# Revit family: CADS_AIRFLOWdev_AirTerminal_SquareExternalGrille_Intake
name_source: partatom
category: Air Terminals
revit_build: Autodesk Revit 2015 (Build: 20160512_0715(x64)
units: mm (PartAtom-declared; Revit-internal decimal feet)

## types (16) — shared parameters
6MonthlyMaintenance = Visually inspect system, clean the fan and ducting if necessary
AirflowRateRange = 0-61
AssetType = Fixed
B = 20 mm  [stored 0.0656168 ft]
CEApproval = Yes
Default Elevation = 1219 mm
DurationUnit = Years
Exclusions = Incorrect Use / Incorrect Installation / Installed by a non-accredited electrician. Customer abuse.
FaceType = LOUVERED
Finish = Matte
FlowControlType = NONE
Grade = Virgin
HasIntegralControl = No
HasSoundAttenuator = No
HasThermalInsulation = No
ISO140001 = Yes
ISO90001 = Yes
IsExtendedWarranty = No
Manufacturer = Airflow Developments Ltd
ManufacturerAddress = Aidelle House
Lancaster Road
Cressex Business Park
High Wycombe
Bucks
HP123QP
ManufacturerTelephone = 01494 525252
ManufacturerWebsite = www.airflow.com
Material = Plastic
MountingType = SURFACE
NBSCode = 90-75-50/370 Air terminals;
PointOfContact = Airflow Developments Ltd
ProductionYear = 2017
ServiceLifeDuration = 10
ServiceLifeType = EXPECTEDSERVICELIFE
Shape = Rectangular
Uniclass2015 = Pr_65_70_46_01
WarrantyContent = Replacement of part if faulty
WarrantyGuarantor = Airflow Developments Ltd
WarrantyPeriod = 2

## per-type parameters (varying)
| type | A | Color | Constituents | D | Description | Dv | External_Grille | Fly_Screen | GrossWeight | ModelLabel | ModelReference | NominalHeight | NominalLength | NominalWidth | NumberOfSlots | ReplacementCost | ShippingWeight | Size |
| 140 x 140 x 100mm Dia - White | 140 mm  [stored 0.459318 ft] | White | White | 100 mm  [stored 0.328084 ft] | 140 x 140 x 100mm dia. Fixed Grille (White) No F/S | 98 mm  [stored 0.321522 ft] | CADS_AirFlow_White | No | 0.01 kg | 140 x 140 x 100mm dia. Fixed Grille (White) No F/S | 52641101 | 140 mm  [stored 0.459318 ft] | 46 mm  [stored 0.150919 ft] | 140 mm  [stored 0.459318 ft] | 20 | 4.752 | 0.01 kg | 46 x 140 x 140 |
| 140 x 140 x 100mm Dia -  Grey | 140 mm  [stored 0.459318 ft] | Grey | Grey | 100 mm  [stored 0.328084 ft] | 140 x 140 x 100mm dia. Fixed Grille (Grey) No F/S | 98 mm  [stored 0.321522 ft] | CADS_AirFlow_Grey | No | 0.01 kg | 140 x 140 x 100mm dia. Fixed Grille (Grey) No F/S | 52641102 | 140 mm  [stored 0.459318 ft] | 46 mm  [stored 0.150919 ft] | 140 mm  [stored 0.459318 ft] | 20 | 4.752 | 0.01 kg | 46 x 140 x 140 |
| 140 x 140 x 100mm Dia - Terracotta | 140 mm  [stored 0.459318 ft] | Terracotta | Terracotta | 100 mm  [stored 0.328084 ft] | 140 x 140 x 100mm dia. Fixed Grille (Terracotta) No F/S | 98 mm  [stored 0.321522 ft] | CADS_AirFlow_Terracotta | No | 0.01 kg | 140 x 140 x 100mm dia. Fixed Grille (Terracotta) No F/S | 52641103 | 140 mm  [stored 0.459318 ft] | 46 mm  [stored 0.150919 ft] | 140 mm  [stored 0.459318 ft] | 20 | 4.752 | 0.01 kg | 46 x 140 x 140 |
| 140 x 140 x 100mm Dia - Brown | 140 mm  [stored 0.459318 ft] | Brown | Brown | 100 mm  [stored 0.328084 ft] | 140 x 140 x 100mm dia. Fixed Grille (Brown) No F/S | 98 mm  [stored 0.321522 ft] | CADS_AirFlow_Brown | No | 0.01 kg | 140 x 140 x 100mm dia. Fixed Grille (Brown) No F/S | 52641104 | 140 mm  [stored 0.459318 ft] | 46 mm  [stored 0.150919 ft] | 140 mm  [stored 0.459318 ft] | 20 | 4.752 | 0.01 kg | 46 x 140 x 140 |
| 140 x 140 x 100mm Dia - Beige | 140 mm  [stored 0.459318 ft] | Beige | Beige | 100 mm  [stored 0.328084 ft] | 140 x 140 x 100mm dia. Fixed Grille (Beige) No F/S | 98 mm  [stored 0.321522 ft] | CADS_AirFlow_Beige | No | 0.01 kg | 140 x 140 x 100mm dia. Fixed Grille (Beige) No F/S | 52641105 | 140 mm  [stored 0.459318 ft] | 46 mm  [stored 0.150919 ft] | 140 mm  [stored 0.459318 ft] | 20 | 4.752 | 0.01 kg | 46 x 140 x 140 |
| 140 x 140 x 100mm Dia - Brown With F/S | 140 mm  [stored 0.459318 ft] | Brown | Brown | 100 mm  [stored 0.328084 ft] | 140 x 140 x 100mm dia. Fixed Grille (Brown) with F/S | 98 mm  [stored 0.321522 ft] | CADS_AirFlow_Brown | Yes | 0.01 kg | 140 x 140 x 100mm dia. Fixed Grille (Brown) with F/S | 9021012 | 140 mm  [stored 0.459318 ft] | 46 mm  [stored 0.150919 ft] | 140 mm  [stored 0.459318 ft] | 20 | 6.348 | 0.01 kg | 46 x 140 x 140 |
| 140 x 140 x 100mm Dia - Terracotta With F/S | 140 mm  [stored 0.459318 ft] | Terracotta | Terracotta | 100 mm  [stored 0.328084 ft] | 140 x 140 x 100mm dia. Fixed Grille (Terracotta) with F/S | 98 mm  [stored 0.321522 ft] | CADS_AirFlow_Terracotta | Yes | 0.01 kg | 140 x 140 x 100mm dia. Fixed Grille (Terracotta) with F/S | 9021082 | 150 mm | 46 mm  [stored 0.150919 ft] | 150 mm | 20 | 6.348 | 0.01 kg | 47 x 140 x 140 |
| 150 x 150 x 100mm Dia - White With F/S | 150 mm | White | White | 100 mm  [stored 0.328084 ft] | 150 x 150 x 100mm dia. Fixed Grille (White) with F/S | 98 mm  [stored 0.321522 ft] | CADS_AirFlow_White | Yes | 0.01 kg | 150 x 150 x 100mm dia. Fixed Grille (White) with F/S | 9021172 | 140 mm  [stored 0.459318 ft] | 46 mm  [stored 0.150919 ft] | 140 mm  [stored 0.459318 ft] | 20 | 7.944 | 0.01 kg | 46 x 150 x 150 |
| 160 x 160 x 125mm Dia -Terracotta | 160 mm  [stored 0.524934 ft] | Terracotta | Terracotta | 125 mm  [stored 0.410105 ft] | 160 x 160 x 125mm dia. Fixed Grille (Terracotta) No F/S | 123 mm  [stored 0.403543 ft] | CADS_AirFlow_Terracotta | No | 0.01 kg | 160 x 160 x 125mm dia. Fixed Grille (Terracotta) No F/S | 9041223 | 160 mm  [stored 0.524934 ft] | 39 mm  [stored 0.127953 ft] | 160 mm  [stored 0.524934 ft] | 62 | 6.828 | 0.01 kg | 39 x 160 x 160 |
| 160 x 160 x 125mm Dia - Brown | 160 mm  [stored 0.524934 ft] | Brown | Brown | 125 mm  [stored 0.410105 ft] | 160 x 160 x 125mm dia. Fixed Grille (Brown) No F/S | 123 mm  [stored 0.403543 ft] | CADS_AirFlow_Brown | No | 0.01 kg | 160 x 160 x 125mm dia. Fixed Grille (Brown) No F/S | 9041222 | 160 mm  [stored 0.524934 ft] | 39 mm  [stored 0.127953 ft] | 160 mm  [stored 0.524934 ft] | 20 | 6.828 | 0.01 kg | 39 x 160 x 160 |
| 160 x 160 x 125mm Dia - White | 160 mm  [stored 0.524934 ft] | White | White | 125 mm  [stored 0.410105 ft] | 160 x 160 x 125mm dia. Fixed Grille (White) No F/S | 123 mm  [stored 0.403543 ft] | CADS_AirFlow_White | No | 0.01 kg | 160 x 160 x 125mm dia. Fixed Grille (White) No F/S | 9041221 | 160 mm  [stored 0.524934 ft] | 39 mm  [stored 0.127953 ft] | 160 mm  [stored 0.524934 ft] | 20 | 6.828 | 0.01 kg | 39 x 160 x 160 |
| 180 x 180 x 150mm Dia - White | 175 mm  [stored 0.574147 ft] | White | White | 150 mm | 180 x 180 x 150mm dia. Fixed Grille (White) | 148 mm  [stored 0.485564 ft] | CADS_AirFlow_White | No | 0.02 kg | 180 x 180 x 150mm dia. Fixed Grille (White) | 52641106 | 180 mm  [stored 0.590551 ft] | 48 mm  [stored 0.15748 ft] | 180 mm  [stored 0.590551 ft] | 20 | 9.528 | 0.02 kg | 48 x 180 x 180 |
| 180 x 180 x 150mm Dia - Grey | 175 mm  [stored 0.574147 ft] | Grey | Grey | 150 mm | 180 x 180 x 150mm dia. Fixed Grille (Grey) | 148 mm  [stored 0.485564 ft] | CADS_AirFlow_Grey | No | 0.02 kg | 180 x 180 x 150mm dia. Fixed Grille (Grey) | 52641107 | 180 mm  [stored 0.590551 ft] | 48 mm  [stored 0.15748 ft] | 180 mm  [stored 0.590551 ft] | 20 | 9.528 | 0.02 kg | 48 x 180 x 180 |
| 180 x 180 x 150mm Dia - Terracotta | 175 mm  [stored 0.574147 ft] | Terracotta | Terracotta | 150 mm | 180 x 180 x 150mm dia. Fixed Grille (Terracotta) | 148 mm  [stored 0.485564 ft] | CADS_AirFlow_Terracotta | No | 0.02 kg | 180 x 180 x 150mm dia. Fixed Grille (Terracotta) | 52641108 | 180 mm  [stored 0.590551 ft] | 48 mm  [stored 0.15748 ft] | 180 mm  [stored 0.590551 ft] | 20 | 9.528 | 0.02 kg | 48 x 180 x 180 |
| 180 x 180 x 150mm Dia - Brown | 175 mm  [stored 0.574147 ft] | Brown | Brown | 150 mm | 180 x 180 x 150mm dia. Fixed Grille (Brown) | 148 mm  [stored 0.485564 ft] | CADS_AirFlow_Brown | No | 0.02 kg | 180 x 180 x 150mm dia. Fixed Grille (Brown) | 52641109 | 180 mm  [stored 0.590551 ft] | 48 mm  [stored 0.15748 ft] | 180 mm  [stored 0.590551 ft] | 20 | 9.528 | 0.02 kg | 48 x 180 x 180 |
| 180 x 180 x 150mm Dia - Beige | 175 mm  [stored 0.574147 ft] | Beige | Beige | 150 mm | 180 x 180 x 150mm dia. Fixed Grille (Beige) | 148 mm  [stored 0.485564 ft] | CADS_AirFlow_Beige | No | 0.02 kg | 180 x 180 x 150mm dia. Fixed Grille (Beige) | 52641110 | 180 mm  [stored 0.590551 ft] | 48 mm  [stored 0.15748 ft] | 180 mm  [stored 0.590551 ft] | 20 | 9.528 | 0.02 kg | 48 x 180 x 180 |

note: [stored X ft] marks values corroborated as IEEE doubles in the binary element streams (Revit-internal decimal feet)

## geometry (parser evidence)
native form markers: Blend x4, Sweep x3
no freeform markers — native parametric forms only
